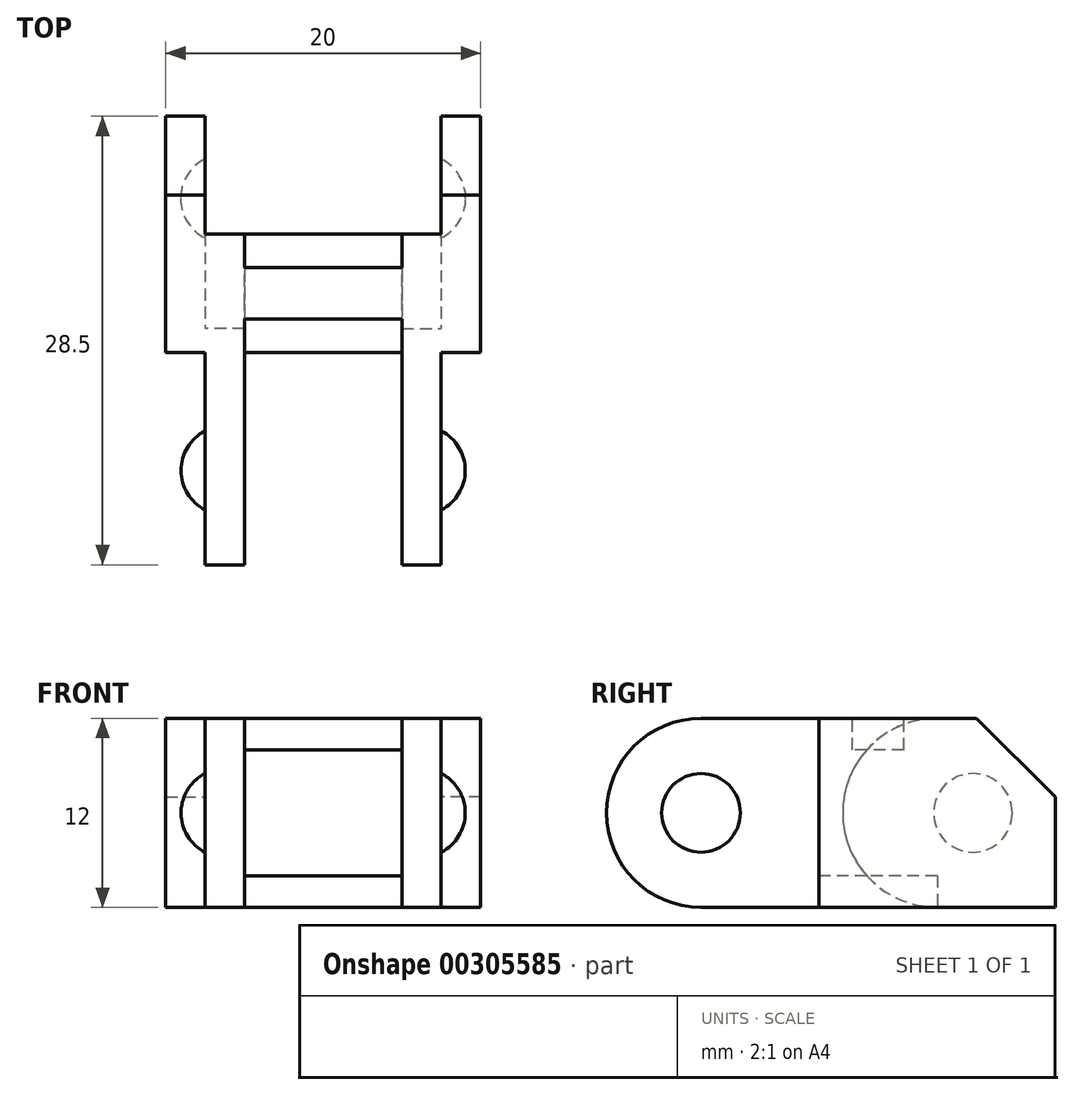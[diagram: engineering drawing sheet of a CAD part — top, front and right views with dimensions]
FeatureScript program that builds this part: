
annotation { "Feature Type Name" : "Feature", "Feature Type Description" : "" }
export const myFeature = defineFeature(function(context is Context, id is Id, definition is map)
    precondition{}
    {
        {
            var Q0;
            Q0=qCreatedBy(makeId("Right.planeOp"),FACE);
            var sketch = newSketch(context, id + "F0", { "sketchPlane" : qUnion([Q0])});
            skLineSegment(sketch, "E0", {"start": v(0, -6) * mm, "end": v(15, -6) * mm});
            skLineSegment(sketch, "E1", {"start": v(0, -6) * mm, "end": v(0, 6) * mm});
            skLineSegment(sketch, "E2", {"start": v(0, 6) * mm, "end": v(10, 6) * mm});
            skLineSegment(sketch, "E3", {"start": v(10, 6) * mm, "end": v(15, 1) * mm});
            skLineSegment(sketch, "E4", {"start": v(15, 1) * mm, "end": v(15, -6) * mm});
            skSolve(sketch);
        }
        {
            var Q0;
            Q0=qCreatedBy(makeId("Right.planeOp"),FACE);
            var sketch = newSketch(context, id + "F1", { "sketchPlane" : qUnion([Q0])});
            skLineSegment(sketch, "E5.0", {"start": v(0, -6) * mm, "end": v(0, 6) * mm, "construction": true});
            skLineSegment(sketch, "E5.1", {"start": v(0, 6) * mm, "end": v(10, 6) * mm, "construction": true});
            skLineSegment(sketch, "E5.2", {"start": v(0, -6) * mm, "end": v(15, -6) * mm, "construction": true});
            skLineSegment(sketch, "E6", {"start": v(10, 7.9) * mm, "end": v(7.5, 7.9) * mm, "construction": true});
            skLineSegment(sketch, "E7", {"start": v(7.5, 6) * mm, "end": v(-7.5, 6) * mm});
            skLineSegment(sketch, "E8", {"start": v(7.5, -6) * mm, "end": v(-7.5, -6) * mm});
            skArc(sketch, "E9", {"start": v(-7.5, 6) * mm, "mid": v(-13.5, 0) * mm, "end": v(-7.5, -6) * mm});
            skArc(sketch, "E10", {"start": v(7.5, -6) * mm, "mid": v(1.5, 0) * mm, "end": v(7.5, 6) * mm});
            skLineSegment(sketch, "E11", {"start": v(-7.5, 8.36) * mm, "end": v(-7.5, -8.68) * mm, "construction": true});
            skLineSegment(sketch, "E12", {"start": v(-15.65, 0) * mm, "end": v(18.02, 0) * mm, "construction": true});
            skArc(sketch, "E13", {"start": v(-10, 0) * mm, "mid": v(-7.5, 2.5) * mm, "end": v(-5, 0) * mm});
            skSolve(sketch);
        }
        {
            var Q0;
            Q0=makeQuery(id+"F1.imprint","IMPRINT",FACE,{"disambiguationData":[TD([[makeQuery(id+"F1.imprint","IMPRINT",EDGE,{"derivedFrom":sQuery(id+"F1.wireOp",EDGE,"E7")}),1.0]])]});
            extrude(context, id + "F2", {"entities" : qUnion([Q0]), "oppositeDirection" : true, "depth" : 2.5 * mm});
        }
        {
            var Q0;
            Q0=makeQuery(id+"F2.opExtrude","CAP_FACE",FACE,{"disambiguationData":[OSD([sQuery(id+"F1.wireOp",EDGE,"E7"),sQuery(id+"F1.wireOp",EDGE,"E8"),sQuery(id+"F1.wireOp",EDGE,"E9"),sQuery(id+"F1.wireOp",EDGE,"E10")])],"isStart":false});
            cPlane(context, id + "F3", {"entities" : qUnion([Q0]), "cplaneType" : CPlaneType.OFFSET, "offset" : 1.25 * mm, "oppositeDirection" : true, "width" : 150 * mm, "height" : 150 * mm});
        }
        {
            var Q0;
            Q0=makeQuery(id+"F0.imprint","IMPRINT",FACE,{"disambiguationData":[TD([[makeQuery(id+"F0.imprint","IMPRINT",EDGE,{"derivedFrom":sQuery(id+"F0.wireOp",EDGE,"E0")}),1.0]])]});
            extrude(context, id + "F4", {"entities" : qUnion([Q0]), "operationType" : NewBodyOperationType.ADD, "depth" : 2.5 * mm});
        }
        {
            var Q0;
            Q0=qCreatedBy(makeId("Front.planeOp"),FACE);
            cPlane(context, id + "F5", {"entities" : qUnion([Q0]), "cplaneType" : CPlaneType.OFFSET, "offset" : 9.77 * mm, "oppositeDirection" : true, "width" : 150 * mm, "height" : 150 * mm});
        }
        {
            var Q0;
            Q0=qCreatedBy(id+"F5.planeOp",FACE);
            var sketch = newSketch(context, id + "F6", { "sketchPlane" : qUnion([Q0])});
            skLineSegment(sketch, "E14", {"start": v(-28.05, 0) * mm, "end": v(6.44, 0) * mm, "construction": true});
            skLineSegment(sketch, "E15", {"start": v(1.5, 7.89) * mm, "end": v(1.5, -13.1) * mm, "construction": true});
            skLineSegment(sketch, "E16", {"start": v(0, 7.89) * mm, "end": v(0, -9.72) * mm, "construction": true});
            skLineSegment(sketch, "E17", {"start": v(-2.53, 0) * mm, "end": v(-2.53, 2.5) * mm});
            skArc(sketch, "E18", {"start": v(0, 2.5) * mm, "mid": v(1.14, 1.47) * mm, "end": v(1.56, 0) * mm});
            skLineSegment(sketch, "E19", {"start": v(0, 2.5) * mm, "end": v(-2.53, 2.5) * mm});
            skLineSegment(sketch, "E20", {"start": v(-2.53, 0) * mm, "end": v(1.56, 0) * mm});
            skSolve(sketch);
        }
        {
            var Q0;
            Q0 = qSketchRegion(id + "F6", true);
            var Q1;
            Q1=sQuery(id+"F6.wireOp",EDGE,"E14");
            revolve(context, id + "F7", {"operationType" : NewBodyOperationType.REMOVE, "entities" : qUnion([Q0]), "axis" : qUnion([Q1]), "revolveType" : RevolveType.FULL, "oppositeDirection" : true});
        }
        {
            var Q0;
            Q0=makeQuery(id+"F4.boolean.opBoolean","MERGE",FACE,{"derivedFrom":[makeQuery(id+"F2.opExtrude","SWEPT_FACE",FACE,{"disambiguationData":[OSD([sQuery(id+"F1.wireOp",EDGE,"E7")])]}),makeQuery(id+"F4.opExtrude","SWEPT_FACE",FACE,{"disambiguationData":[OSD([sQuery(id+"F0.wireOp",EDGE,"E2")])]})]});
            var sketch = newSketch(context, id + "F8", { "sketchPlane" : qUnion([Q0])});
            skLineSegment(sketch, "E21.0", {"start": v(-2.5, 7.5) * mm, "end": v(0, 7.5) * mm, "construction": true});
            skLineSegment(sketch, "E21.1", {"start": v(2.5, 0) * mm, "end": v(0, 0) * mm, "construction": true});
            skLineSegment(sketch, "E22", {"start": v(-5, 7.5) * mm, "end": v(-5, 0) * mm, "construction": true});
            skPoint(sketch, "E22.endSnap0", {"position": v(-2.5, 0) * mm});
            skLineSegment(sketch, "E23", {"start": v(-10.67, 3.75) * mm, "end": v(12.8, 3.75) * mm, "construction": true});
            skPoint(sketch, "E23.startSnap0", {"position": v(-5, 3.75) * mm});
            skLineSegment(sketch, "E24.bottom", {"start": v(-7.5, 5.38) * mm, "end": v(-2.49, 5.38) * mm});
            skLineSegment(sketch, "E24.top", {"start": v(-7.5, 2.12) * mm, "end": v(-2.49, 2.12) * mm});
            skLineSegment(sketch, "E24.left", {"start": v(-7.5, 5.38) * mm, "end": v(-7.5, 2.12) * mm});
            skLineSegment(sketch, "E24.right", {"start": v(-2.49, 5.38) * mm, "end": v(-2.49, 2.12) * mm});
            skSolve(sketch);
        }
        {
            var Q0;
            {var subQ0=sQuery(id+"F8.wireOp",EDGE,"E24.left");Q0=makeQuery(id+"F8.imprint","IMPRINT",FACE,{"disambiguationData":[TD([[makeQuery(id+"F8.imprint","IMPRINT",EDGE,{"derivedFrom":subQ0}),1.0]])]});}
            extrude(context, id + "F9", {"entities" : qUnion([Q0]), "operationType" : NewBodyOperationType.ADD, "oppositeDirection" : true, "depth" : 2 * mm});
        }
        {
            var Q0;
            Q0=makeQuery(id+"F4.boolean.opBoolean","MERGE",FACE,{"derivedFrom":[makeQuery(id+"F2.opExtrude","SWEPT_FACE",FACE,{"disambiguationData":[OSD([sQuery(id+"F1.wireOp",EDGE,"E8")])]}),makeQuery(id+"F4.opExtrude","SWEPT_FACE",FACE,{"disambiguationData":[OSD([sQuery(id+"F0.wireOp",EDGE,"E0")])]})]});
            var sketch = newSketch(context, id + "F10", { "sketchPlane" : qUnion([Q0])});
            skPoint(sketch, "E25.0", {"position": v(-7.5, -3.75) * mm});
            skLineSegment(sketch, "E26", {"start": v(-11.22, -3.75) * mm, "end": v(4.98, -3.75) * mm, "construction": true});
            skLineSegment(sketch, "E27.0", {"start": v(-2.5, -7.5) * mm, "end": v(0, -7.5) * mm, "construction": true});
            skLineSegment(sketch, "E27.1", {"start": v(2.5, 0) * mm, "end": v(0, 0) * mm, "construction": true});
            skPoint(sketch, "E27.2", {"position": v(-5, -5.38) * mm});
            skLineSegment(sketch, "E28.bottom", {"start": v(-7.5, -7.5) * mm, "end": v(-2.5, -7.5) * mm});
            skLineSegment(sketch, "E28.top", {"start": v(-7.5, 0) * mm, "end": v(-2.5, 0) * mm});
            skLineSegment(sketch, "E28.left", {"start": v(-7.5, -7.5) * mm, "end": v(-7.5, 0) * mm});
            skLineSegment(sketch, "E28.right", {"start": v(-2.5, -7.5) * mm, "end": v(-2.5, 0) * mm});
            skSolve(sketch);
        }
        {
            var Q0;
            Q0=makeQuery(id+"F10.imprint","IMPRINT",FACE,{"disambiguationData":[TD([[makeQuery(id+"F10.imprint","IMPRINT",EDGE,{"derivedFrom":sQuery(id+"F10.wireOp",EDGE,"E28.bottom")}),1.0]])]});
            extrude(context, id + "F11", {"entities" : qUnion([Q0]), "operationType" : NewBodyOperationType.ADD, "oppositeDirection" : true, "depth" : 2 * mm});
        }
        {
            var Q0;
            Q0=makeQuery(id+"F11.opExtrude","SWEPT_FACE",FACE,{"disambiguationData":[OSD([sQuery(id+"F10.wireOp",EDGE,"E28.left")])]});
            cPlane(context, id + "F12", {"entities" : qUnion([Q0]), "cplaneType" : CPlaneType.OFFSET, "offset" : 0 * mm, "width" : 150 * mm, "height" : 150 * mm});
        }
        {
            var Q0;
            Q0=makeQuery(id+"F4.opExtrude","SWEPT_FACE",FACE,{"disambiguationData":[OSD([sQuery(id+"F0.wireOp",EDGE,"E1")])]});
            cPlane(context, id + "F13", {"entities" : qUnion([Q0]), "cplaneType" : CPlaneType.OFFSET, "offset" : 7.5 * mm, "width" : 150 * mm, "height" : 150 * mm});
        }
        {
            var Q0;
            Q0=qCreatedBy(id+"F13.planeOp",FACE);
            var sketch = newSketch(context, id + "F14", { "sketchPlane" : qUnion([Q0])});
            skLineSegment(sketch, "E29", {"start": v(-5.3, 0) * mm, "end": v(4.83, 0) * mm, "construction": true});
            skArc(sketch, "E30", {"start": v(1.52, 0) * mm, "mid": v(1.11, 1.46) * mm, "end": v(0, 2.5) * mm});
            skLineSegment(sketch, "E31", {"start": v(0, 2.5) * mm, "end": v(0, 0) * mm});
            skLineSegment(sketch, "E32", {"start": v(0, 0) * mm, "end": v(1.52, 0) * mm});
            skSolve(sketch);
        }
        {
            var Q0;
            Q0=makeQuery(id+"F14.imprint","IMPRINT",FACE,{"disambiguationData":[TD([[makeQuery(id+"F14.imprint","IMPRINT",EDGE,{"derivedFrom":sQuery(id+"F14.wireOp",EDGE,"E30")}),1.0]])]});
            var Q1;
            Q1=sQuery(id+"F14.wireOp",EDGE,"E29");
            revolve(context, id + "F15", {"operationType" : NewBodyOperationType.ADD, "entities" : qUnion([Q0]), "axis" : qUnion([Q1]), "revolveType" : RevolveType.FULL});
        }
        {
            var Q0;
            Q0=makeQuery(id+"F2.opExtrude","SWEPT_BODY",BODY,{"disambiguationData":[OSD([sQuery(id+"F1.wireOp",EDGE,"E7"),sQuery(id+"F1.wireOp",EDGE,"E8"),sQuery(id+"F1.wireOp",EDGE,"E9"),sQuery(id+"F1.wireOp",EDGE,"E10")])]});
            var Q1;
            Q1=qCreatedBy(id+"F12.planeOp",FACE);
            mirror(context, id + "F16", {"operationType" : NewBodyOperationType.ADD, "entities" : qUnion([Q0]), "mirrorPlane" : qUnion([Q1])});
        }
    });
